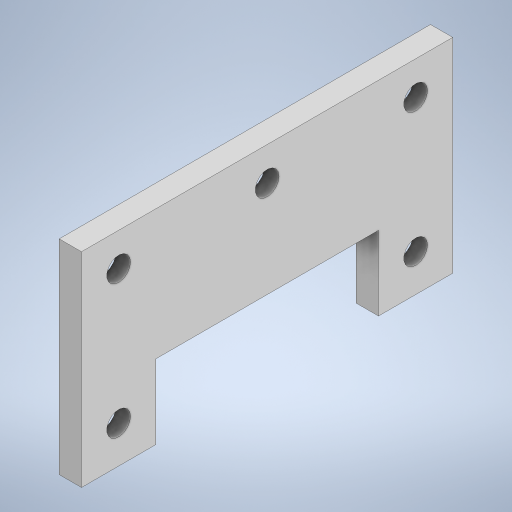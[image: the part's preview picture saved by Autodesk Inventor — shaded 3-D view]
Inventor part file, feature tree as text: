
AUTODESK INVENTOR PART (.ipt)
format: ipt  version: 2023 (Build 270158000, 158)  size: 255,488 bytes
history: native  units: mm
features: sketch x5, extrude x4, other x1, hole x1
ambient origin geometry x8: Origin, YZ Plane, XZ Plane, XY Plane, X Axis, Y Axis, Z Axis, Center Point
bodies: Body1 (feature_tree)
feature tree (11):
  other  "ソリッド1"
  extrude  "押し出し1"  Depth=10.0mm
  hole  "穴1"  [1 undecoded]
  extrude  "押し出し2"  Depth=17.5mm
  extrude  "押し出し3"  Depth=3.0mm TaperAngle=0.0deg
  extrude  "押し出し4"  Depth=40.0mm
  sketch  "スケッチ1"
  sketch  "スケッチ2"
  sketch  "スケッチ3"
  sketch  "スケッチ4"
  sketch  "スケッチ5"
note: 1 required parameter value undecoded (feature->parameter linkage not recoverable at this tier; creation-order binding heuristic only, values carry confidence <= 0.55)
